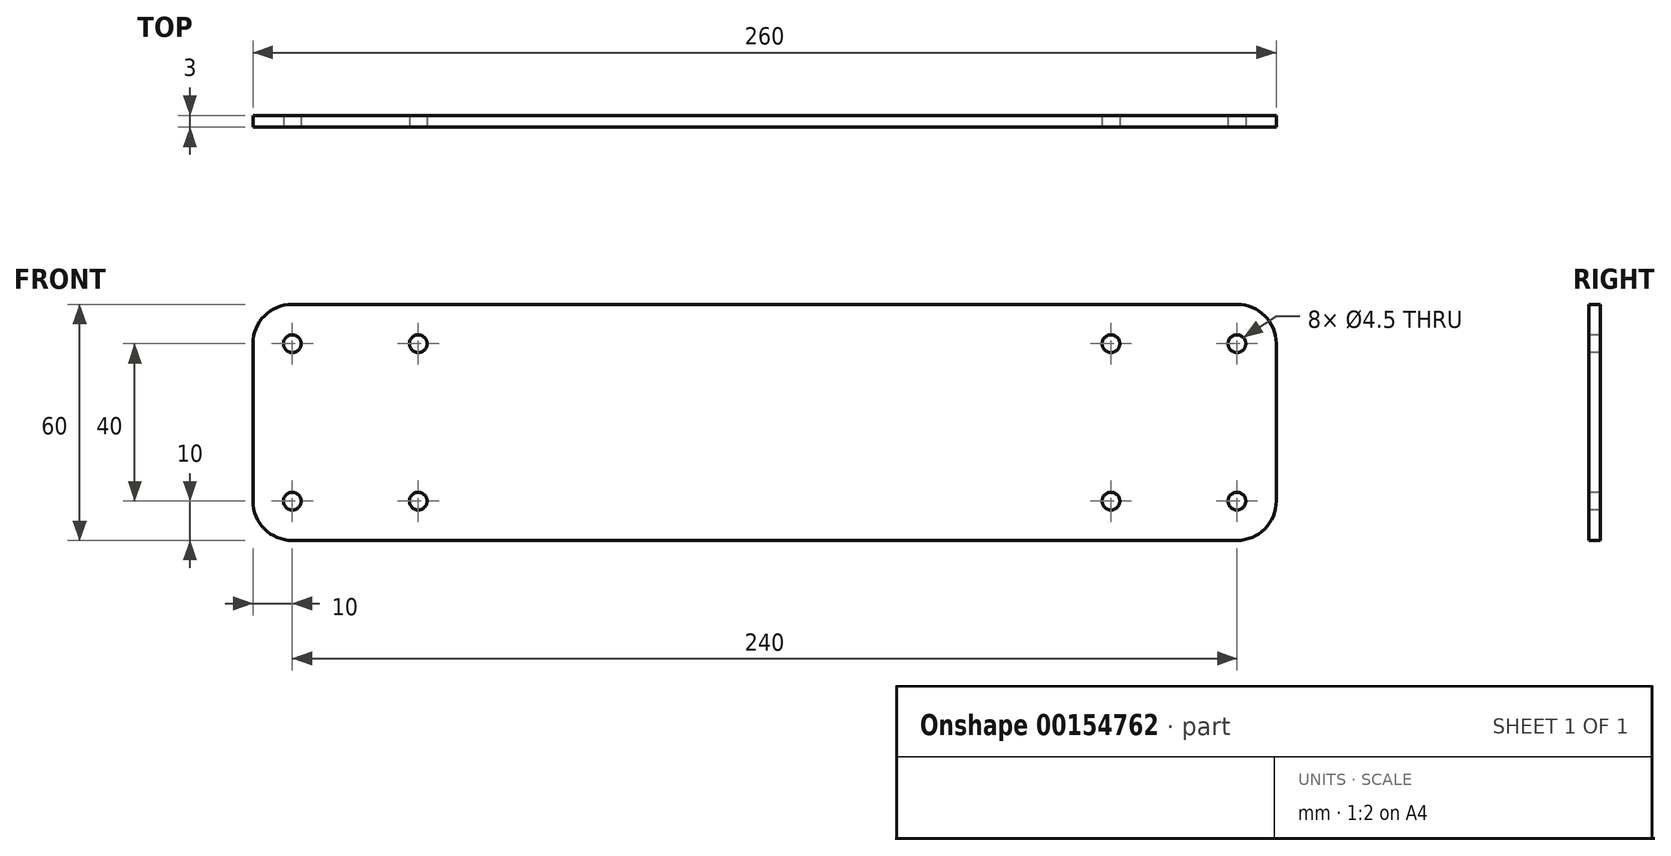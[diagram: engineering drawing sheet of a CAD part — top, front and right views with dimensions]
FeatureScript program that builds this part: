
annotation { "Feature Type Name" : "Feature", "Feature Type Description" : "" }
export const myFeature = defineFeature(function(context is Context, id is Id, definition is map)
    precondition{}
    {
        {
            var Q0;
            Q0=qCreatedBy(makeId("Front.planeOp"),FACE);
            var sketch = newSketch(context, id + "F0", { "sketchPlane" : qUnion([Q0])});
            skLineSegment(sketch, "E0.bottom", {"start": v(130, -30) * mm, "end": v(-130, -30) * mm});
            skLineSegment(sketch, "E0.top", {"start": v(130, 30) * mm, "end": v(-130, 30) * mm});
            skLineSegment(sketch, "E0.left", {"start": v(130, -30) * mm, "end": v(130, 30) * mm});
            skLineSegment(sketch, "E0.right", {"start": v(-130, -30) * mm, "end": v(-130, 30) * mm});
            skPoint(sketch, "E0.middle", {"position": v(0, 0) * mm});
            skSolve(sketch);
        }
        {
            var Q0;
            Q0 = qSketchRegion(id + "F0", true);
            extrude(context, id + "F1", {"entities" : qUnion([Q0]), "depth" : 3 * mm});
        }
        {
            var Q0;
            Q0=makeQuery(id+"F1.opExtrude","CAP_FACE",FACE,{"disambiguationData":[OSD([sQuery(id+"F0.wireOp",EDGE,"E0.bottom"),sQuery(id+"F0.wireOp",EDGE,"E0.top"),sQuery(id+"F0.wireOp",EDGE,"E0.left"),sQuery(id+"F0.wireOp",EDGE,"E0.right")])],"isStart":false});
            var sketch = newSketch(context, id + "F2", { "sketchPlane" : qUnion([Q0])});
            skCircle(sketch, "E1", {"center": v(-120, 20) * mm, "radius": 2.25 * mm});
            skCircle(sketch, "E2.0.1.0", {"center": v(-120, -20) * mm, "radius": 2.25 * mm});
            skCircle(sketch, "E2.1.0.0", {"center": v(-88, 20) * mm, "radius": 2.25 * mm});
            skCircle(sketch, "E2.1.1.0", {"center": v(-88, -20) * mm, "radius": 2.25 * mm});
            skLineSegment(sketch, "E2.direction1", {"start": v(-120, 20) * mm, "end": v(-88, 20) * mm, "construction": true});
            skLineSegment(sketch, "E2.direction2", {"start": v(-120, 20) * mm, "end": v(-120, -20) * mm, "construction": true});
            skLineSegment(sketch, "E3", {"start": v(0, 30) * mm, "end": v(0, -30) * mm});
            skCircle(sketch, "E4.MirrorC", {"center": v(88, 20) * mm, "radius": 2.25 * mm});
            skCircle(sketch, "E5.MirrorC", {"center": v(120, 20) * mm, "radius": 2.25 * mm});
            skCircle(sketch, "E6.MirrorC", {"center": v(120, -20) * mm, "radius": 2.25 * mm});
            skCircle(sketch, "E7.MirrorC", {"center": v(88, -20) * mm, "radius": 2.25 * mm});
            skSolve(sketch);
        }
        {
            var Q0;
            Q0 = qSketchRegion(id + "F2", true);
            extrude(context, id + "F3", {"entities" : qUnion([Q0]), "operationType" : NewBodyOperationType.REMOVE, "endBound" : BoundingType.THROUGH_ALL, "oppositeDirection" : true, "depth" : 25 * mm});
        }
        {
            var Q0;
            Q0=makeQuery(id+"F1.opExtrude","SWEPT_EDGE",EDGE,{"disambiguationData":[OSD([sQuery(id+"F0.wireOp",EDGE,"E0.top"),sQuery(id+"F0.wireOp",EDGE,"E0.right")])]});
            var Q1;
            Q1=makeQuery(id+"F1.opExtrude","SWEPT_EDGE",EDGE,{"disambiguationData":[OSD([sQuery(id+"F0.wireOp",EDGE,"E0.bottom"),sQuery(id+"F0.wireOp",EDGE,"E0.right")])]});
            var Q2;
            Q2=makeQuery(id+"F1.opExtrude","SWEPT_EDGE",EDGE,{"disambiguationData":[OSD([sQuery(id+"F0.wireOp",EDGE,"E0.bottom"),sQuery(id+"F0.wireOp",EDGE,"E0.left")])]});
            var Q3;
            Q3=makeQuery(id+"F1.opExtrude","SWEPT_EDGE",EDGE,{"disambiguationData":[OSD([sQuery(id+"F0.wireOp",EDGE,"E0.top"),sQuery(id+"F0.wireOp",EDGE,"E0.left")])]});
            fillet(context, id + "F4", {"entities" : qUnion([Q0, Q1, Q2, Q3]), "radius" : 10 * mm, "tangentPropagation" : true, "allowEdgeOverflow" : false});
        }
    });
